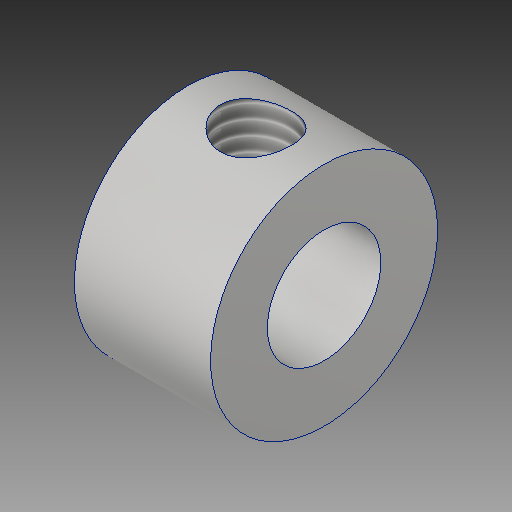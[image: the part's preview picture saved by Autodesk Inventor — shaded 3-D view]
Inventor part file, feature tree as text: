
AUTODESK INVENTOR PART (.ipt)
format: ipt  version: 2019 (Build 230136000, 136)  size: 130,048 bytes
history: native  units: in
note: dims shown in document units (in); Inventor stores cm internally (conversion verified against a paired STEP export)
features: other x3, sketch x2, plane x1
ambient origin geometry x8: Origin, YZ Plane, XZ Plane, XY Plane, X Axis, Y Axis, Z Axis, Center Point
bodies: Solid1 (feature_tree)
feature tree (6):
  other  "Collar.ipt"
  other  "Solid2::Collar.ipt"
  other  "TaggingFeature1"
  sketch  "Sketch2"  dims[d0=0.3937in]
  sketch  "Sketch3"
  plane  "Work Plane1"
